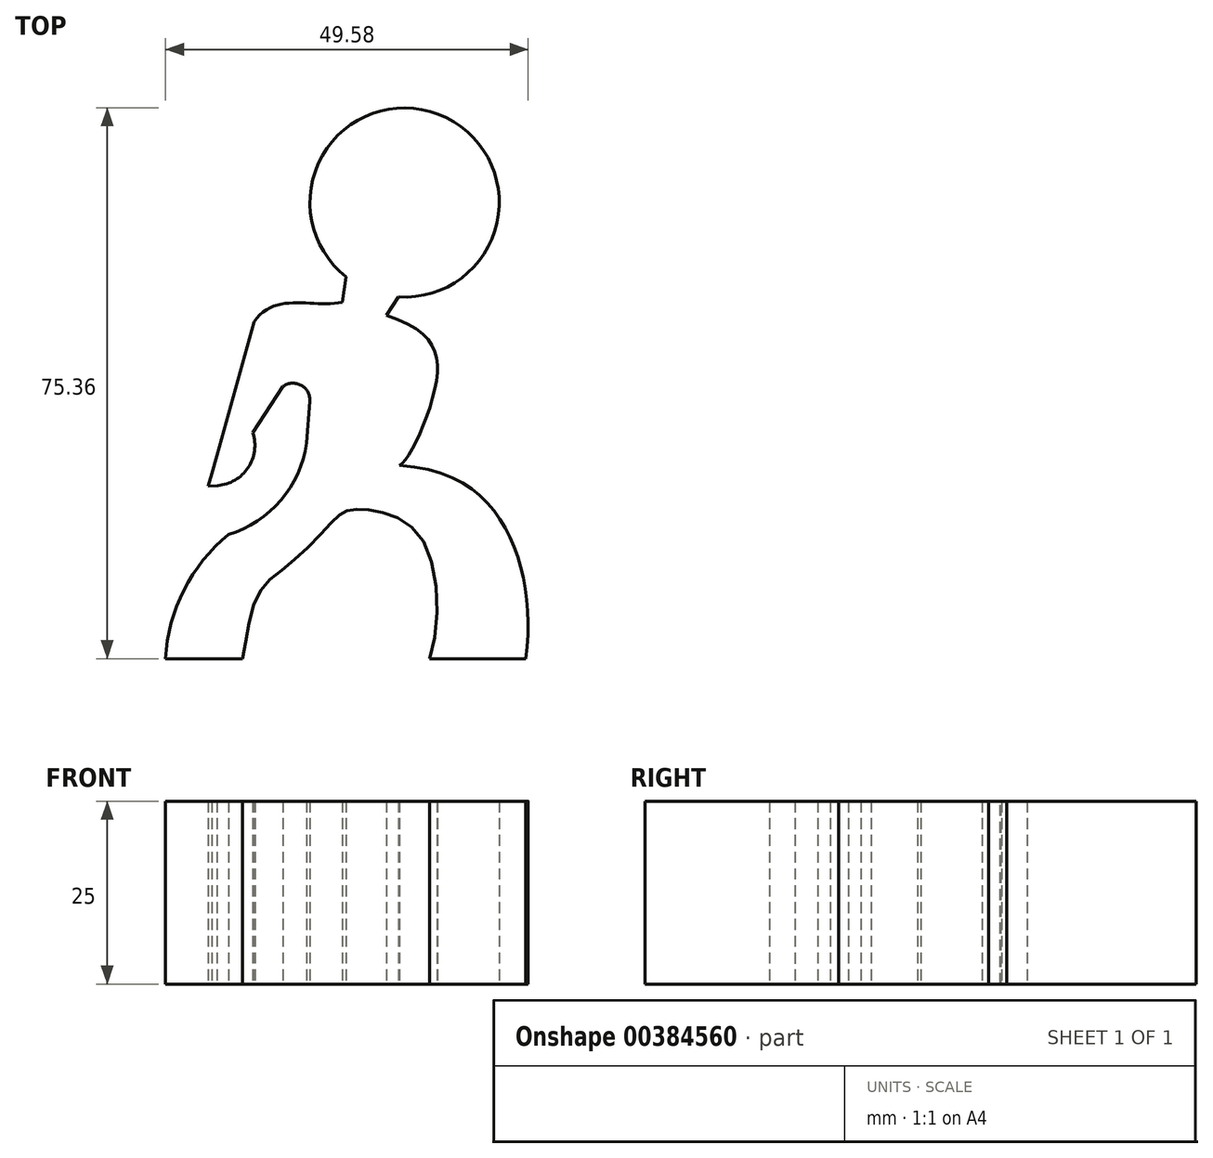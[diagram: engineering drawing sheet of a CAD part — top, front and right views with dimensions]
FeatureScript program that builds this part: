
annotation { "Feature Type Name" : "Feature", "Feature Type Description" : "" }
export const myFeature = defineFeature(function(context is Context, id is Id, definition is map)
    precondition{}
    {
        {
            var Q0;
            Q0=qCreatedBy(makeId("Top.planeOp"),FACE);
            var sketch = newSketch(context, id + "F0", { "sketchPlane" : qUnion([Q0])});
            skArc(sketch, "E0", {"start": v(8.59, 16.99) * mm, "mid": v(2.5, 9.4) * mm, "end": v(0, 0) * mm});
            skArc(sketch, "E1", {"start": v(8.59, 16.99) * mm, "mid": v(15.76, 21.68) * mm, "end": v(19.28, 29.49) * mm});
            skArc(sketch, "E2", {"start": v(7.13, 23.69) * mm, "mid": v(11.27, 26.13) * mm, "end": v(11.93, 30.9) * mm});
            skLineSegment(sketch, "E3", {"start": v(7.13, 23.69) * mm, "end": v(5.82, 23.58) * mm});
            skLineSegment(sketch, "E4", {"start": v(5.82, 23.58) * mm, "end": v(6.3, 25.34) * mm});
            skLineSegment(sketch, "E5", {"start": v(7.05, 27.78) * mm, "end": v(12.07, 46.09) * mm});
            skPoint(sketch, "E6.visualSharp", {"position": v(13.3, 50.58) * mm});
            skFitSpline(sketch, "E7", {"points": [v(31.96, 26.48) * mm, v(36.97, 37.7) * mm, v(30.17, 47) * mm], "startDerivative": vector(8.08, 3.23) * mm, "endDerivative": vector(-39.25, 13.33) * mm});
            skFitSpline(sketch, "E8", {"points": [v(31.96, 26.48) * mm, v(46.75, 17.3) * mm, v(49.25, 0) * mm], "startDerivative": vector(49.98, -3.79) * mm, "endDerivative": vector(-5.27, -38.55) * mm});
            skLineSegment(sketch, "E9", {"start": v(49.25, 0) * mm, "end": v(36.13, 0) * mm});
            skLineSegment(sketch, "E10", {"start": v(0, 0) * mm, "end": v(10.53, 0) * mm});
            skFitSpline(sketch, "E11", {"points": [v(10.53, 0) * mm, v(12.63, 8.8) * mm, v(17.36, 13.32) * mm, v(23.07, 19) * mm, v(25.08, 20.3) * mm, v(29.1, 20.15) * mm, v(35.42, 15.74) * mm, v(36.13, 0) * mm], "startDerivative": vector(10.65, 48.85) * mm, "endDerivative": vector(-19.97, -58.3) * mm});
            skPoint(sketch, "E12.endSnap0", {"position": v(19.27, 48.66) * mm});
            skLineSegment(sketch, "E13", {"start": v(24.14, 48.78) * mm, "end": v(24.68, 52.25) * mm});
            skLineSegment(sketch, "E14", {"start": v(30.17, 47) * mm, "end": v(31.84, 49.5) * mm});
            skArc(sketch, "E15", {"start": v(31.84, 49.5) * mm, "mid": v(37.31, 74.5) * mm, "end": v(24.68, 52.25) * mm});
            skLineSegment(sketch, "E16", {"start": v(6.3, 25.34) * mm, "end": v(7.05, 27.78) * mm});
            skLineSegment(sketch, "E17", {"start": v(11.93, 30.9) * mm, "end": v(16.06, 37.25) * mm});
            skLineSegment(sketch, "E18", {"start": v(19.72, 35.2) * mm, "end": v(19.28, 29.49) * mm});
            skPoint(sketch, "E19.visualSharp", {"position": v(16.83, 38.44) * mm});
            skPoint(sketch, "E20.visualSharp", {"position": v(19.6, 33.5) * mm});
            skArc(sketch, "E21", {"start": v(19.72, 35.2) * mm, "mid": v(18.55, 37.4) * mm, "end": v(16.06, 37.25) * mm});
            skFitSpline(sketch, "E22", {"points": [v(12.07, 46.09) * mm, v(24.14, 48.78) * mm], "startDerivative": vector(8.84, 12.74) * mm, "endDerivative": vector(12.07, 2.69) * mm});
            skSolve(sketch);
        }
        {
            var Q0;
            Q0 = qSketchRegion(id + "F0", true);
            extrude(context, id + "F1", {"entities" : qUnion([Q0]), "depth" : 25 * mm});
        }
    });
